# Revit family: Dali Side Chair Uph
name_source: partatom
category: Arredi
revit_build: Autodesk Revit 2017 (Build: 20160225_1515(x64)
units: mm (PartAtom-declared; Revit-internal decimal feet)

## family parameters
Basato su piano di lavoro = No
Condiviso = No
Numero OmniClass = 23.40.20.00
Punto di calcolo locali = No
Sempre verticale = Sì
Taglio con vuoti quando caricato = No
Titolo OmniClass = General Furniture and Specialties

## types (1)
- Dali Side Chair Uph
    Assistance = Call for assistance number: 336.941.3446
    Chair type = Side
    Codice assieme = E2020200
    Collection = Dali
    Commenti sul tipo = Suitable for use in Cafeteria, Church, Dining, Hospitality, Institutional, Office, University
    Depth = 19 mm
    Descrizione = Fully upholstered chair with tapered mixing metal and wood legs
    Height = 34 mm
    Industry = Café, Restaurant, Bistro, Hotel, Club, College
    Manufacturer Country = USA
    Modello = Dali Side Chair Uph
    Products of collection = Dali Side Chair, Laminate, Pad, Pronto and Dali Barstool Wood Veneer, Laminate, Padded seat, Pronto, Uph
    Produttore = Beaufurn
    Seat height = 19 mm
    Structure material = Standard wood finishes or COF
    URL = https://beaufurn.com
    Upholstery material = Graded Fabric or COM
    Usage = Indoor
    Wight = 17 mm
    Yardage = 1.5
